# Revit family: 306_H6_W_-S7
name_source: partatom
category: Pipe Accessories
units: mm (PartAtom-declared; Revit-internal decimal feet)

## family parameters
Always vertical = Yes
Cut with Voids When Loaded = No
Part Type = Valve - Breaks Into
Round Connector Dimension = Use Diameter
Shared = No
Work Plane-Based = No

## types (2) — shared parameters
CAT0 = Yes
Description = Globe valve, 2-way, Flange, PN 16
L2D_Min = 3048 mm  [stored 10 ft]
Manufacturer = Belimo
QmdConnectorList = 301;D;302;D
magiPartTypeId = 306
magiProductFamilyId = H6*W*-S7
zero-valued in all types: MC_Default_elevation

## per-type parameters (varying)
| type | B | C | C__ve | D | DM | DM2 | DR | DT | FD | H | HM | HM1 | HM2 | L2 | L2D | LM | W2D |
| H6200W630-S7 | 187 mm  [stored 0.613517 ft] | 30 mm  [stored 0.0984252 ft] | -30 mm  [stored -0.0984252 ft] | 200 mm | 287 mm | 230 mm | 100 mm  [stored 0.328084 ft] | 350 mm  [stored 1.14829 ft] | 340 mm  [stored 1.11549 ft] | 315 mm  [stored 1.03346 ft] | 158 mm | 79 mm | 47 mm | 300 mm  [stored 0.984252 ft] | 600 mm | 540 mm  [stored 1.77165 ft] | 200 mm  [stored 0.656168 ft] |
| H6250W1000-S7 | 233 mm  [stored 0.764436 ft] | 32 mm  [stored 0.104987 ft] | -32 mm  [stored -0.104987 ft] | 250 mm | 356 mm | 285 mm  [stored 0.935039 ft] | 125 mm  [stored 0.410105 ft] | 438 mm | 405 mm  [stored 1.32874 ft] | 375 mm  [stored 1.23031 ft] | 188 mm | 94 mm | 56 mm | 365 mm  [stored 1.19751 ft] | 730 mm | 666 mm  [stored 2.18504 ft] | 250 mm  [stored 0.82021 ft] |

note: column(s) folded — value = type name in every type: magiProductCode, magiProductId

note: [stored X ft] marks values corroborated as IEEE doubles in the binary element streams (Revit-internal decimal feet)

## geometry (parser evidence)
native form markers: Sweep x2
no freeform markers — native parametric forms only
